# Revit family: 207_Kombiboks Black _
name_source: partatom
category: Air Terminals
revit_build: Autodesk Revit 2018 (Build: 20170223_1515(x64)
units: mm (PartAtom-declared; Revit-internal decimal feet)

## family parameters
Always vertical = Yes
Cut with Voids When Loaded = No
Part Type = Normal
Room Calculation Point = Yes
Round Connector Dimension = Use Diameter
Shared = No
Work Plane-Based = No

## types (5) — shared parameters
CAT0 = Yes
CL_Location_5000 = 5000 mm
Description = Wall hood V13 black  part 1 of 2
L_ARR = 400 mm
Manufacturer = Flexit
QmdConnectorList = 201;D
W_ARR = 400 mm
X = 2 mm  [stored 0.00656168 ft]
magiPartTypeId = 207
magiProductFamilyId = Kombiboks Black *
zero-valued in all types: CLBTZ, H_ARR

## per-type parameters (varying)
| type | A1 | A2 | B4T2 | BT2 | D | E2 | F | G | W1 | X1 | Z | ZA | magiProductId |
| 125-112727 | 238 mm  [stored 0.78084 ft] | 127 mm  [stored 0.416667 ft] | 115 mm  [stored 0.377297 ft] | 230 mm  [stored 0.754593 ft] | 125 mm | 63 mm | 127 mm  [stored 0.416667 ft] | 105 mm  [stored 0.344488 ft] | 185 mm  [stored 0.606955 ft] | 123 mm  [stored 0.403543 ft] | 13 mm | 212 mm | Kombiboks Black 125 |
| 160-112729 | 280 mm  [stored 0.918635 ft] | 148 mm | 120 mm  [stored 0.393701 ft] | 240 mm  [stored 0.787402 ft] | 160 mm | 63 mm | 147 mm  [stored 0.482283 ft] | 110 mm  [stored 0.360892 ft] | 220 mm  [stored 0.721785 ft] | 123 mm  [stored 0.403543 ft] | 15 mm  [stored 0.0492126 ft] | 250 mm  [stored 0.82021 ft] | Kombiboks Black 160 |
| 200-112731 | 318 mm  [stored 1.04331 ft] | 167 mm  [stored 0.5479 ft] | 149 mm  [stored 0.488845 ft] | 298 mm  [stored 0.97769 ft] | 200 mm | 63 mm | 167 mm  [stored 0.5479 ft] | 120 mm  [stored 0.393701 ft] | 260 mm  [stored 0.853018 ft] | 123 mm  [stored 0.403543 ft] | 15 mm  [stored 0.0492126 ft] | 289 mm  [stored 0.948163 ft] | Kombiboks Black 200 |
| 250-112733 | 445 mm | 230 mm  [stored 0.754593 ft] | 195 mm  [stored 0.639764 ft] | 390 mm | 250 mm | 93 mm | 231 mm  [stored 0.757874 ft] | 175 mm  [stored 0.574147 ft] | 310 mm  [stored 1.01706 ft] | 183 mm  [stored 0.600394 ft] | 34 mm | 378 mm | Kombiboks Black 250 |
| 315-112734 | 535 mm | 275 mm  [stored 0.902231 ft] | 235 mm  [stored 0.770997 ft] | 470 mm | 315 mm | 125 mm  [stored 0.410105 ft] | 275 mm  [stored 0.902231 ft] | 210 mm  [stored 0.688976 ft] | 375 mm | 248 mm  [stored 0.813648 ft] | 40 mm  [stored 0.131234 ft] | 455 mm | Kombiboks Black 315 |

note: column(s) folded — value = type name in every type: MC Product Code

note: [stored X ft] marks values corroborated as IEEE doubles in the binary element streams (Revit-internal decimal feet)

## geometry (parser evidence)
native form markers: Sweep x2
no freeform markers — native parametric forms only
